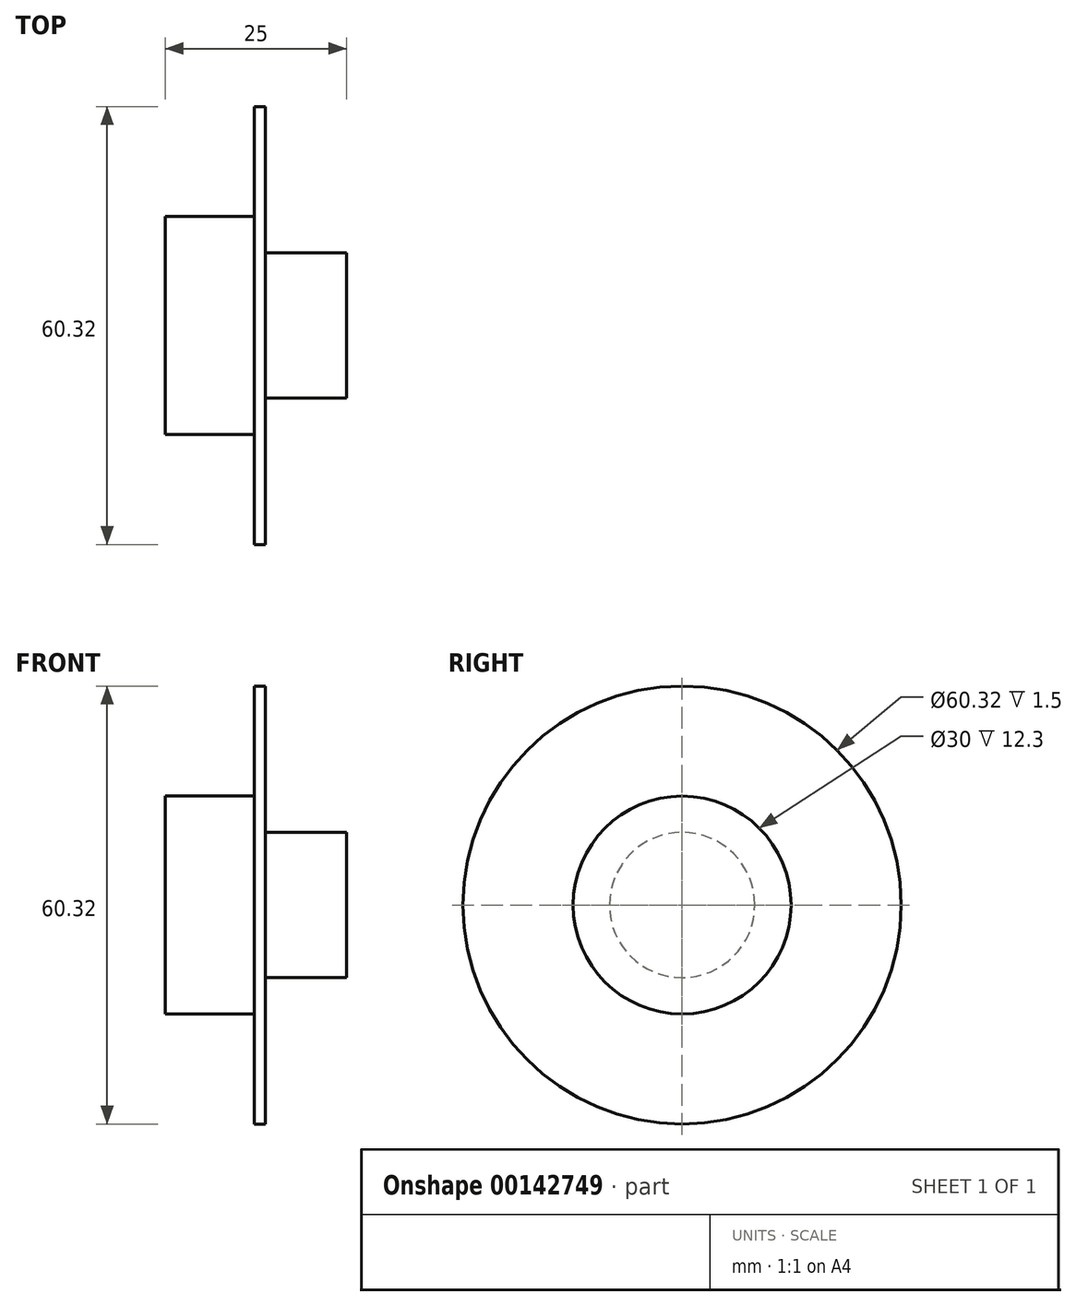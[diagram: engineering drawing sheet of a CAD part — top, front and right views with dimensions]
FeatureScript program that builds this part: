
annotation { "Feature Type Name" : "Feature", "Feature Type Description" : "" }
export const myFeature = defineFeature(function(context is Context, id is Id, definition is map)
    precondition{}
    {
        {
            var Q0;
            Q0=qCreatedBy(makeId("Top.planeOp"),FACE);
            var sketch = newSketch(context, id + "F0", { "sketchPlane" : qUnion([Q0])});
            skLineSegment(sketch, "E0", {"start": v(0, 0) * mm, "end": v(0, 15) * mm});
            skLineSegment(sketch, "E1", {"start": v(0, 15) * mm, "end": v(12.3, 15) * mm});
            skLineSegment(sketch, "E2", {"start": v(12.3, 15) * mm, "end": v(12.3, 30.16) * mm});
            skLineSegment(sketch, "E3", {"start": v(12.3, 30.16) * mm, "end": v(13.8, 30.16) * mm});
            skLineSegment(sketch, "E4", {"start": v(13.8, 30.16) * mm, "end": v(13.8, 10) * mm});
            skLineSegment(sketch, "E5", {"start": v(13.8, 10) * mm, "end": v(25, 10) * mm});
            skLineSegment(sketch, "E6", {"start": v(25, 10) * mm, "end": v(25, 0) * mm});
            skLineSegment(sketch, "E7", {"start": v(0, 0) * mm, "end": v(39.05, 0) * mm, "construction": true});
            skSolve(sketch);
        }
        {
            var Q0;
            Q0=sQuery(id+"F0.wireOp",EDGE,"E1");
            var Q1;
            Q1=sQuery(id+"F0.wireOp",EDGE,"E0");
            var Q2;
            Q2=sQuery(id+"F0.wireOp",EDGE,"E2");
            var Q3;
            Q3=sQuery(id+"F0.wireOp",EDGE,"E3");
            var Q4;
            Q4=sQuery(id+"F0.wireOp",EDGE,"E4");
            var Q5;
            Q5=sQuery(id+"F0.wireOp",EDGE,"E5");
            var Q6;
            Q6=sQuery(id+"F0.wireOp",EDGE,"E6");
            var Q7;
            Q7=sQuery(id+"F0.wireOp",EDGE,"E7");
            revolve(context, id + "F1", {"bodyType" : ToolBodyType.SURFACE, "surfaceEntities" : qUnion([Q0, Q1, Q2, Q3, Q4, Q5, Q6]), "axis" : qUnion([Q7]), "revolveType" : RevolveType.FULL});
        }
    });
